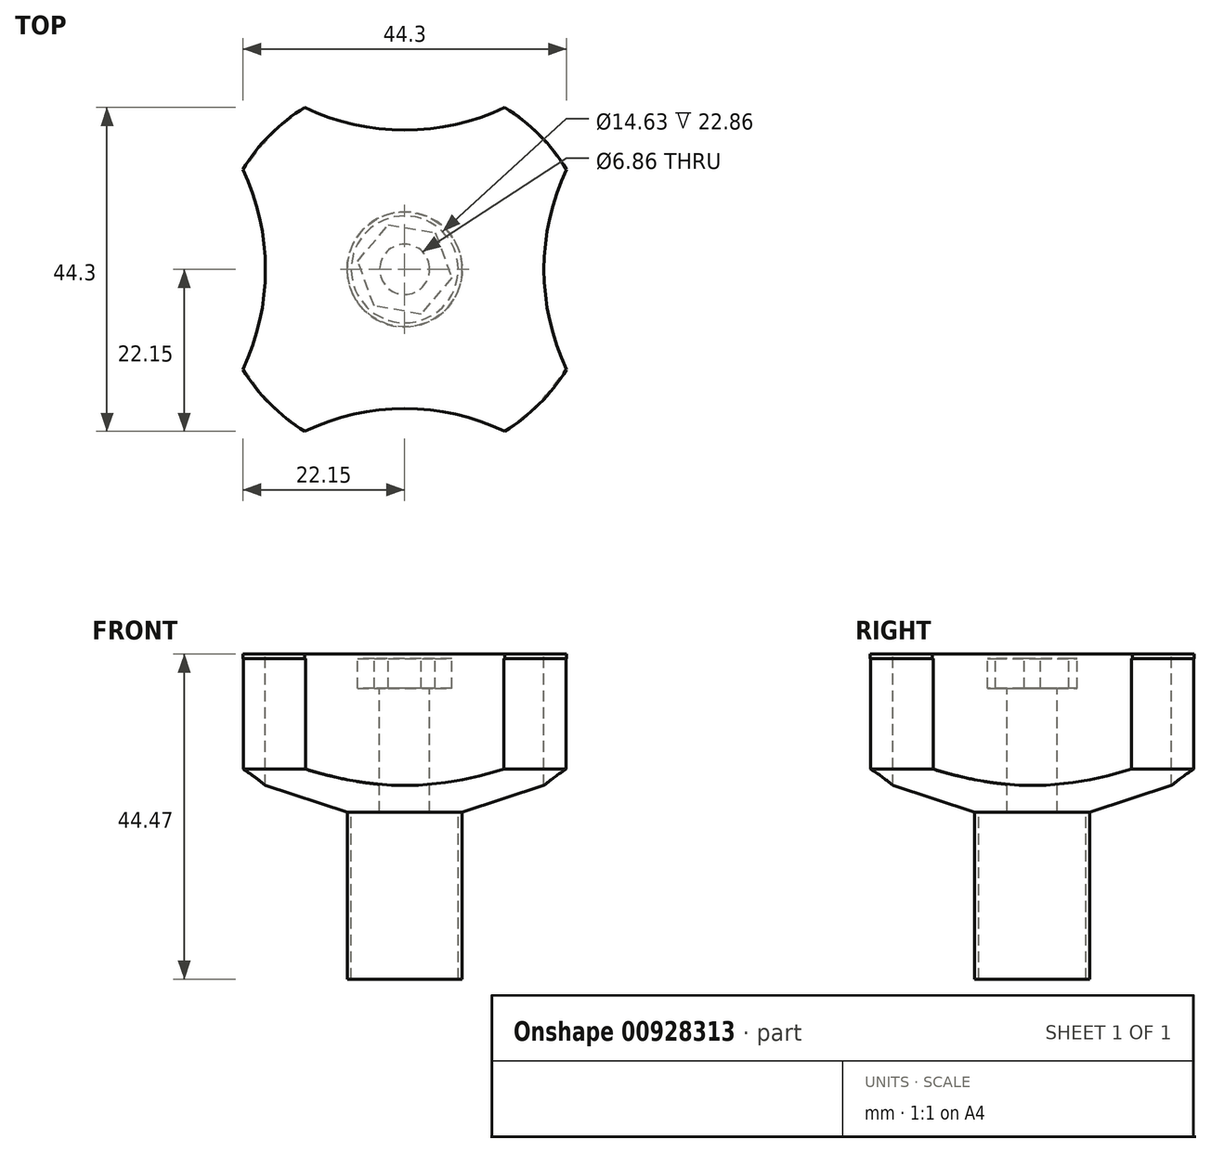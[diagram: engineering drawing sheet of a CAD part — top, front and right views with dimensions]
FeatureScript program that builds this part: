
annotation { "Feature Type Name" : "Feature", "Feature Type Description" : "" }
export const myFeature = defineFeature(function(context is Context, id is Id, definition is map)
    precondition{}
    {
        {
            var Q0;
            Q0=qCreatedBy(makeId("Front.planeOp"),FACE);
            var sketch = newSketch(context, id + "F0", { "sketchPlane" : qUnion([Q0])});
            skLineSegment(sketch, "E0", {"start": v(0, 0) * mm, "end": v(7.87, 0) * mm});
            skLineSegment(sketch, "E1", {"start": v(25.9, 5.86) * mm, "end": v(25.9, 21.6) * mm});
            skLineSegment(sketch, "E2", {"start": v(25.9, 21.6) * mm, "end": v(0, 21.6) * mm});
            skLineSegment(sketch, "E3", {"start": v(0, 21.6) * mm, "end": v(0, 0) * mm});
            skLineSegment(sketch, "E4", {"start": v(7.87, 0) * mm, "end": v(25.9, 5.86) * mm});
            skSolve(sketch);
        }
        {
            var Q0;
            Q0 = qSketchRegion(id + "F0", true);
            var Q1;
            Q1=sQuery(id+"F0.wireOp",EDGE,"E3");
            revolve(context, id + "F1", {"surfaceOperationType" : NewSurfaceOperationType.NEW, "entities" : qUnion([Q0]), "axis" : qUnion([Q1]), "revolveType" : RevolveType.FULL});
        }
        {
            var Q0;
            Q0=makeQuery(id+"F1.opRevolve","SWEPT_FACE",FACE,{"disambiguationData":[OSD([sQuery(id+"F0.wireOp",EDGE,"E2")])]});
            var sketch = newSketch(context, id + "F2", { "sketchPlane" : qUnion([Q0])});
            skCircle(sketch, "E5", {"center": v(0, 0) * mm, "radius": 26.13 * mm});
            skSolve(sketch);
        }
        {
            var Q0;
            Q0 = qSketchRegion(id + "F2", true);
            extrude(context, id + "F3", {"entities" : qUnion([Q0]), "operationType" : NewBodyOperationType.REMOVE, "oppositeDirection" : true, "depth" : 0.64 * mm, "offsetDistance" : 25.4 * mm});
        }
        {
            var Q0;
            Q0=makeQuery(id+"F3.boolean.opBoolean","COPY",FACE,{"derivedFrom":makeQuery(id+"F3.opExtrude","CAP_FACE",FACE,{"disambiguationData":[OSD([sQuery(id+"F2.wireOp",EDGE,"E5")])],"isStart":false})});
            var sketch = newSketch(context, id + "F4", { "sketchPlane" : qUnion([Q0])});
            skCircle(sketch, "E6.cCircle", {"center": v(0, 0) * mm, "radius": 5.65 * mm, "construction": true});
            skLineSegment(sketch, "E6.0", {"start": v(6.43, -1.12) * mm, "end": v(2.24, -6.13) * mm});
            skLineSegment(sketch, "E6.1", {"start": v(2.24, -6.13) * mm, "end": v(-4.19, -5) * mm});
            skLineSegment(sketch, "E6.2", {"start": v(-4.19, -5) * mm, "end": v(-6.43, 1.12) * mm});
            skLineSegment(sketch, "E6.3", {"start": v(-6.43, 1.12) * mm, "end": v(-2.24, 6.13) * mm});
            skLineSegment(sketch, "E6.4", {"start": v(-2.24, 6.13) * mm, "end": v(4.19, 5) * mm});
            skLineSegment(sketch, "E6.5", {"start": v(4.19, 5) * mm, "end": v(6.43, -1.12) * mm});
            skPoint(sketch, "E6.0.midPoint", {"position": v(4.34, -3.62) * mm});
            skSolve(sketch);
        }
        {
            var Q0;
            Q0 = qSketchRegion(id + "F4", true);
            extrude(context, id + "F5", {"entities" : qUnion([Q0]), "operationType" : NewBodyOperationType.REMOVE, "oppositeDirection" : true, "depth" : 4.06 * mm, "offsetDistance" : 25.4 * mm});
        }
        {
            var Q0;
            Q0=makeQuery(id+"F5.boolean.opBoolean","COPY",FACE,{"derivedFrom":makeQuery(id+"F5.opExtrude","CAP_FACE",FACE,{"disambiguationData":[OSD([sQuery(id+"F4.wireOp",EDGE,"E6.0"),sQuery(id+"F4.wireOp",EDGE,"E6.1"),sQuery(id+"F4.wireOp",EDGE,"E6.2"),sQuery(id+"F4.wireOp",EDGE,"E6.3"),sQuery(id+"F4.wireOp",EDGE,"E6.4"),sQuery(id+"F4.wireOp",EDGE,"E6.5")])],"isStart":false})});
            var sketch = newSketch(context, id + "F6", { "sketchPlane" : qUnion([Q0])});
            skCircle(sketch, "E7", {"center": v(0, 0) * mm, "radius": 3.43 * mm});
            skSolve(sketch);
        }
        {
            var Q0;
            Q0 = qSketchRegion(id + "F6", true);
            extrude(context, id + "F7", {"entities" : qUnion([Q0]), "operationType" : NewBodyOperationType.REMOVE, "oppositeDirection" : true, "depth" : 25.4 * mm, "offsetDistance" : 25.4 * mm});
        }
        {
            var Q0;
            Q0=makeQuery(id+"F3.boolean.opBoolean","COPY",FACE,{"derivedFrom":makeQuery(id+"F3.opExtrude","CAP_FACE",FACE,{"disambiguationData":[OSD([sQuery(id+"F2.wireOp",EDGE,"E5")])],"isStart":false})});
            var sketch = newSketch(context, id + "F8", { "sketchPlane" : qUnion([Q0])});
            skCircle(sketch, "E8", {"center": v(0, 0) * mm, "radius": 26.04 * mm});
            skSolve(sketch);
        }
        {
            var Q0;
            Q0 = qSketchRegion(id + "F8", true);
            extrude(context, id + "F9", {"entities" : qUnion([Q0]), "operationType" : NewBodyOperationType.ADD, "depth" : 0.64 * mm, "offsetDistance" : 25.4 * mm});
        }
        {
            var Q0;
            Q0=makeQuery(id+"F1.opRevolve","SWEPT_FACE",FACE,{"disambiguationData":[OSD([sQuery(id+"F0.wireOp",EDGE,"E0")])]});
            var sketch = newSketch(context, id + "F10", { "sketchPlane" : qUnion([Q0])});
            skCircle(sketch, "E9", {"center": v(0, 0) * mm, "radius": 7.87 * mm});
            skCircle(sketch, "E10", {"center": v(0, 0) * mm, "radius": 7.32 * mm});
            skSolve(sketch);
        }
        {
            var Q0;
            Q0 = qSketchRegion(id + "F10", true);
            extrude(context, id + "F11", {"entities" : qUnion([Q0]), "operationType" : NewBodyOperationType.ADD, "depth" : 22.86 * mm, "offsetDistance" : 25.4 * mm});
        }
        {
            var Q0;
            Q0=makeQuery(id+"F9.opExtrude","CAP_FACE",FACE,{"disambiguationData":[OSD([sQuery(id+"F8.wireOp",EDGE,"E8")])],"isStart":false});
            var sketch = newSketch(context, id + "F12", { "sketchPlane" : qUnion([Q0])});
            skCircle(sketch, "E11", {"center": v(-50.8, 0) * mm, "radius": 31.75 * mm});
            skCircle(sketch, "E12", {"center": v(0, 50.8) * mm, "radius": 31.75 * mm});
            skCircle(sketch, "E13", {"center": v(50.8, 0) * mm, "radius": 31.75 * mm});
            skCircle(sketch, "E14", {"center": v(0, -50.8) * mm, "radius": 31.75 * mm});
            skSolve(sketch);
        }
        {
            var Q0;
            Q0 = qSketchRegion(id + "F12", true);
            extrude(context, id + "F13", {"entities" : qUnion([Q0]), "operationType" : NewBodyOperationType.REMOVE, "oppositeDirection" : true, "depth" : 25.4 * mm, "offsetDistance" : 25.4 * mm});
        }
    });
